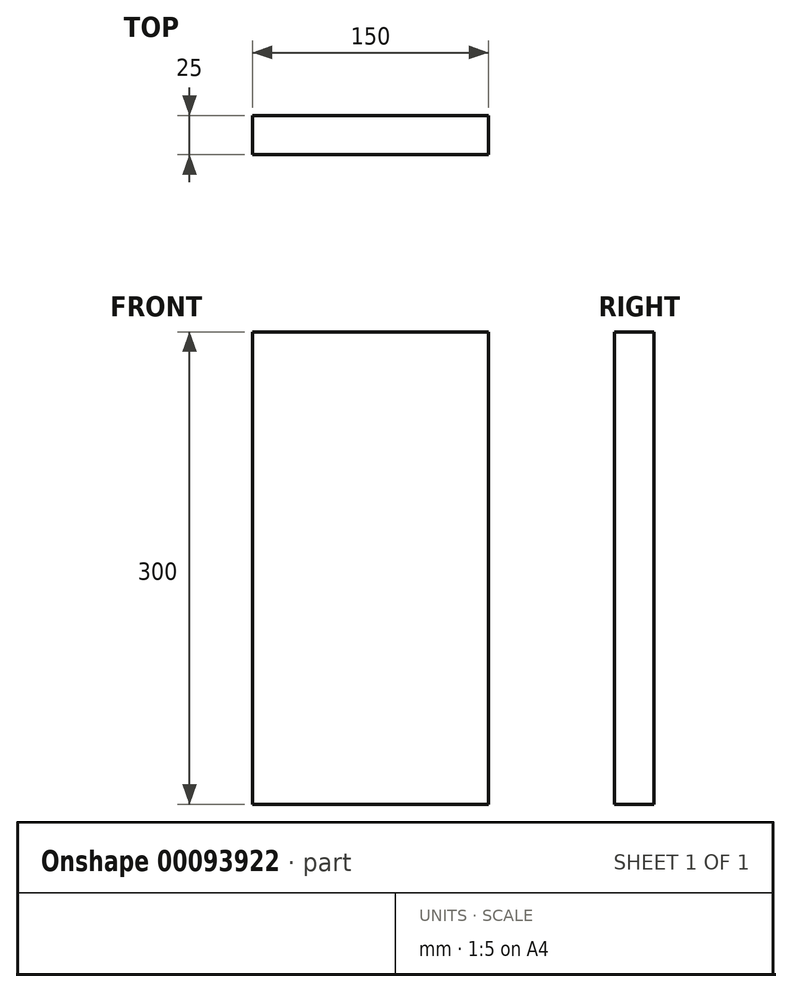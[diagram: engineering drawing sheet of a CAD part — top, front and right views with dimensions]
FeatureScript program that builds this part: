
annotation { "Feature Type Name" : "Feature", "Feature Type Description" : "" }
export const myFeature = defineFeature(function(context is Context, id is Id, definition is map)
    precondition{}
    {
        {
            var Q0;
            Q0=qCreatedBy(makeId("Front.planeOp"),FACE);
            var sketch = newSketch(context, id + "F0", { "sketchPlane" : qUnion([Q0])});
            skLineSegment(sketch, "E0.bottom", {"start": v(-66.74, 264.15) * mm, "end": v(83.26, 264.15) * mm});
            skLineSegment(sketch, "E0.top", {"start": v(-66.74, -35.85) * mm, "end": v(83.26, -35.85) * mm});
            skLineSegment(sketch, "E0.left", {"start": v(-66.74, 264.15) * mm, "end": v(-66.74, -35.85) * mm});
            skLineSegment(sketch, "E0.right", {"start": v(83.26, 264.15) * mm, "end": v(83.26, -35.85) * mm});
            skSolve(sketch);
        }
        {
            var Q0;
            Q0 = qSketchRegion(id + "F0", true);
            extrude(context, id + "F1", {"entities" : qUnion([Q0]), "depth" : 25 * mm});
        }
    });
